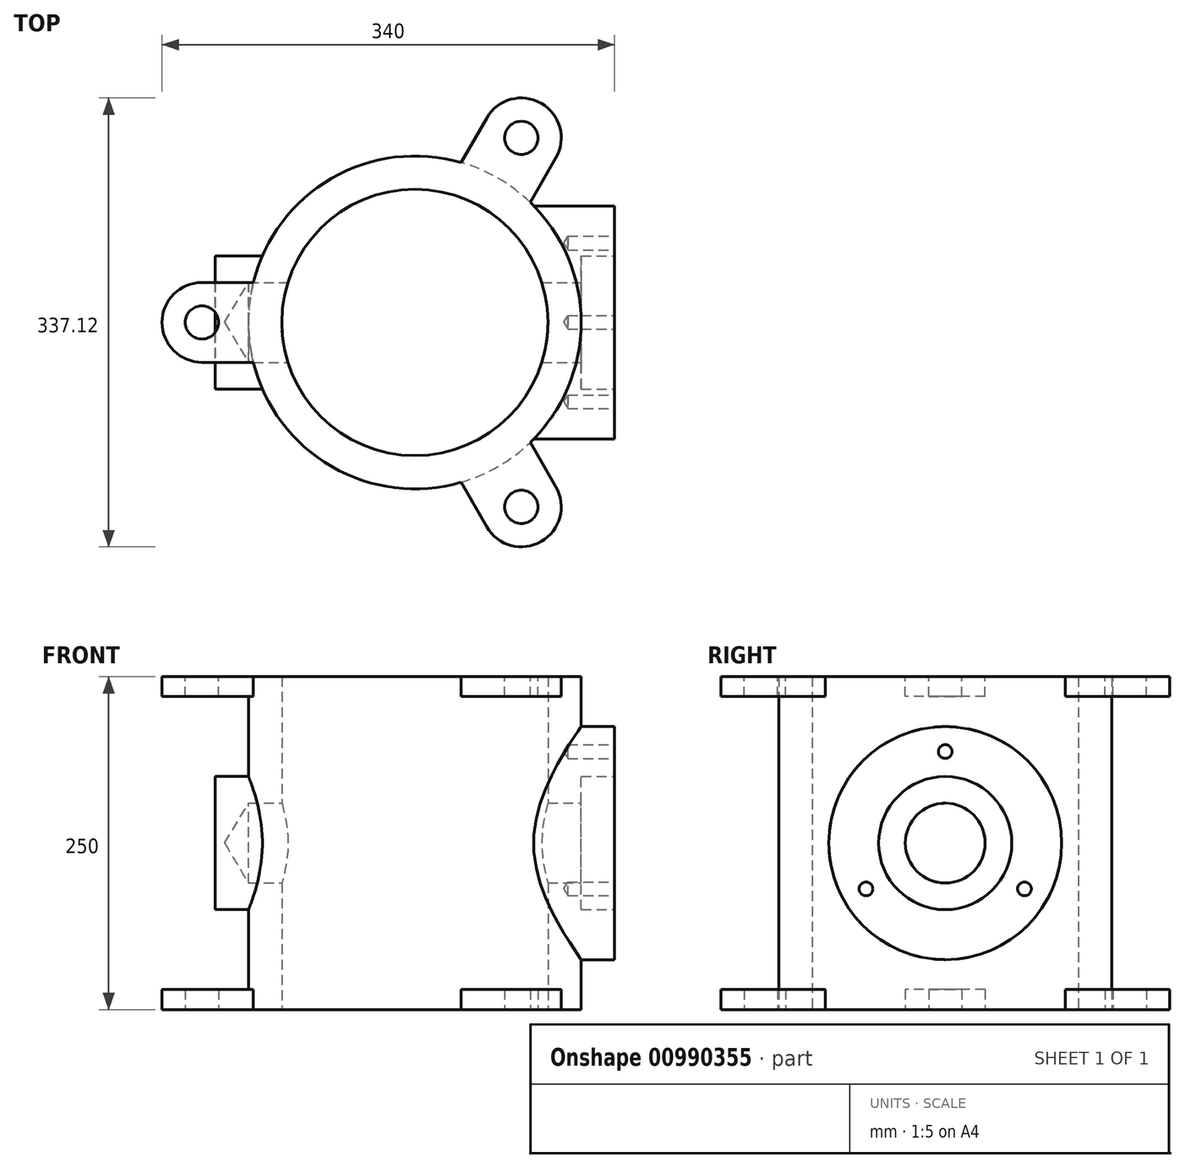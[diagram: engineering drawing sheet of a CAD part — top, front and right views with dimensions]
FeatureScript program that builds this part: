
annotation { "Feature Type Name" : "Feature", "Feature Type Description" : "" }
export const myFeature = defineFeature(function(context is Context, id is Id, definition is map)
    precondition{}
    {
        {
            var Q0;
            Q0=qCreatedBy(makeId("Top.planeOp"),FACE);
            cPlane(context, id + "F0", {"entities" : qUnion([Q0]), "cplaneType" : CPlaneType.OFFSET, "offset" : 125 * mm, "width" : 150 * mm, "height" : 150 * mm});
        }
        {
            var Q0;
            Q0=qCreatedBy(id+"F0.planeOp",FACE);
            var sketch = newSketch(context, id + "F1", { "sketchPlane" : qUnion([Q0])});
            skCircle(sketch, "E0", {"center": v(0, 0) * mm, "radius": 100 * mm});
            skCircle(sketch, "E1", {"center": v(0, 0) * mm, "radius": 125 * mm});
            skCircle(sketch, "E2", {"center": v(0, 0) * mm, "radius": 160 * mm, "construction": true});
            skLineSegment(sketch, "E3", {"start": v(0, 0) * mm, "end": v(-160, 0) * mm, "construction": true});
            skCircle(sketch, "E4", {"center": v(-160, 0) * mm, "radius": 12.5 * mm});
            skArc(sketch, "E5", {"start": v(-160, -30) * mm, "mid": v(-190, 0) * mm, "end": v(-160, 30) * mm});
            skLineSegment(sketch, "E6", {"start": v(-160, 0) * mm, "end": v(-160, 30) * mm, "construction": true});
            skLineSegment(sketch, "E7", {"start": v(-160, 30) * mm, "end": v(-95.4, 30) * mm});
            skLineSegment(sketch, "E8.MirrorCS", {"start": v(-160, -30) * mm, "end": v(-95.4, -30) * mm});
            skCircle(sketch, "E9.1.0", {"center": v(80, -138.56) * mm, "radius": 12.5 * mm});
            skLineSegment(sketch, "E9.1.1", {"start": v(105.98, -123.56) * mm, "end": v(73.68, -67.61) * mm});
            skArc(sketch, "E9.1.2", {"start": v(105.98, -123.56) * mm, "mid": v(95, -164.54) * mm, "end": v(54.02, -153.56) * mm});
            skLineSegment(sketch, "E9.1.3", {"start": v(54.02, -153.56) * mm, "end": v(21.72, -97.61) * mm});
            skCircle(sketch, "E9.2.0", {"center": v(80, 138.56) * mm, "radius": 12.5 * mm});
            skLineSegment(sketch, "E9.2.1", {"start": v(54.02, 153.56) * mm, "end": v(21.72, 97.61) * mm});
            skArc(sketch, "E9.2.2", {"start": v(54.02, 153.56) * mm, "mid": v(95, 164.54) * mm, "end": v(105.98, 123.56) * mm});
            skLineSegment(sketch, "E9.2.3", {"start": v(105.98, 123.56) * mm, "end": v(73.68, 67.61) * mm});
            skSolve(sketch);
        }
        {
            var Q0;
            Q0=qCreatedBy(makeId("Top.planeOp"),FACE);
            var sketch = newSketch(context, id + "F2", { "sketchPlane" : qUnion([Q0])});
            skCircle(sketch, "E10", {"center": v(0, 0) * mm, "radius": 100 * mm});
            skCircle(sketch, "E11", {"center": v(0, 0) * mm, "radius": 125 * mm});
            skSolve(sketch);
        }
        {
            var Q0;
            Q0=makeQuery(id+"F2.imprint","IMPRINT",FACE,{"disambiguationData":[TD([[makeQuery(id+"F2.imprint","IMPRINT",EDGE,{"derivedFrom":sQuery(id+"F2.wireOp",EDGE,"E10")}),-1.0]])]});
            extrude(context, id + "F3", {"entities" : qUnion([Q0]), "endBound" : BoundingType.SYMMETRIC, "depth" : 250 * mm, "offsetDistance" : 25 * mm});
        }
        {
            var Q0;
            Q0 = qSketchRegion(id + "F1", true);
            extrude(context, id + "F4", {"entities" : qUnion([Q0]), "operationType" : NewBodyOperationType.ADD, "oppositeDirection" : true, "depth" : 15 * mm, "offsetDistance" : 25 * mm});
        }
        {
            var Q0;
            Q0=makeQuery(id+"F3.opExtrude","SWEPT_BODY",BODY,{"disambiguationData":[OSD([sQuery(id+"F2.wireOp",EDGE,"E10"),sQuery(id+"F2.wireOp",EDGE,"E11")])]});
            var Q1;
            Q1=qCreatedBy(makeId("Top.planeOp"),FACE);
            mirror(context, id + "F5", {"operationType" : NewBodyOperationType.ADD, "entities" : qUnion([Q0]), "mirrorPlane" : qUnion([Q1])});
        }
        {
            var Q0;
            Q0=qCreatedBy(makeId("Right.planeOp"),FACE);
            cPlane(context, id + "F6", {"entities" : qUnion([Q0]), "cplaneType" : CPlaneType.OFFSET, "offset" : 150 * mm, "width" : 150 * mm, "height" : 150 * mm});
        }
        {
            var Q0;
            Q0=qCreatedBy(id+"F6.planeOp",FACE);
            var sketch = newSketch(context, id + "F7", { "sketchPlane" : qUnion([Q0])});
            skCircle(sketch, "E12", {"center": v(0, 0) * mm, "radius": 87.5 * mm});
            skCircle(sketch, "E13", {"center": v(0, 0) * mm, "radius": 68.75 * mm, "construction": true});
            skCircle(sketch, "E14", {"center": v(0, 0) * mm, "radius": 50 * mm});
            skCircle(sketch, "E15", {"center": v(0, 0) * mm, "radius": 30 * mm});
            skLineSegment(sketch, "E16", {"start": v(0, 0) * mm, "end": v(0, 68.75) * mm, "construction": true});
            skPoint(sketch, "E17", {"position": v(0, 68.75) * mm});
            skPoint(sketch, "E18.1.0", {"position": v(-59.54, -34.37) * mm});
            skPoint(sketch, "E18.2.0", {"position": v(59.54, -34.38) * mm});
            skSolve(sketch);
        }
        {
            var Q0;
            Q0=makeQuery(id+"F7.imprint","IMPRINT",FACE,{"disambiguationData":[TD([[makeQuery(id+"F7.imprint","IMPRINT",EDGE,{"derivedFrom":sQuery(id+"F7.wireOp",EDGE,"E14")}),1.0]])]});
            var Q1;
            Q1=makeQuery(id+"F7.imprint","IMPRINT",FACE,{"disambiguationData":[TD([[makeQuery(id+"F7.imprint","IMPRINT",EDGE,{"derivedFrom":sQuery(id+"F7.wireOp",EDGE,"E12")}),1.0]])]});
            extrude(context, id + "F8", {"entities" : qUnion([Q0, Q1]), "operationType" : NewBodyOperationType.ADD, "endBound" : BoundingType.UP_TO_NEXT, "oppositeDirection" : true, "depth" : 25 * mm, "offsetDistance" : 25 * mm});
        }
        {
            var Q0;
            Q0=makeQuery(id+"F7.imprint","IMPRINT",FACE,{"disambiguationData":[TD([[makeQuery(id+"F7.imprint","IMPRINT",EDGE,{"derivedFrom":sQuery(id+"F7.wireOp",EDGE,"E14")}),1.0]])]});
            extrude(context, id + "F9", {"entities" : qUnion([Q0]), "operationType" : NewBodyOperationType.REMOVE, "oppositeDirection" : true, "depth" : 25 * mm, "offsetDistance" : 25 * mm});
        }
        {
            var Q0;
            Q0=sQuery(id+"F7.wireOp",VERTEX,"E17");
            var Q1;
            Q1=sQuery(id+"F7.wireOp",VERTEX,"E18.2.0");
            var Q2;
            Q2=sQuery(id+"F7.wireOp",VERTEX,"E18.1.0");
            var Q3;
            Q3=makeQuery(id+"F3.opExtrude","SWEPT_BODY",BODY,{"disambiguationData":[OSD([sQuery(id+"F2.wireOp",EDGE,"E10"),sQuery(id+"F2.wireOp",EDGE,"E11")])]});
            hole(context, id + "F10", {"style" : HoleStyle.SIMPLE, "endStyle" : HoleEndStyle.BLIND, "holeDiameter" : 10.3 * mm, "majorDiameter" : 5 * mm, "holeDepth" : 35 * mm, "isTappedThrough" : true, "tappedDepth" : 12 * mm, "tapClearance" : 3, "locations" : qUnion([Q0, Q1, Q2]), "scope" : qUnion([Q3])});
        }
        {
            var Q0;
            Q0=qCreatedBy(makeId("Right.planeOp"),FACE);
            cPlane(context, id + "F11", {"entities" : qUnion([Q0]), "cplaneType" : CPlaneType.OFFSET, "offset" : 150 * mm, "oppositeDirection" : true, "width" : 150 * mm, "height" : 150 * mm});
        }
        {
            var Q0;
            Q0=qCreatedBy(id+"F11.planeOp",FACE);
            var sketch = newSketch(context, id + "F12", { "sketchPlane" : qUnion([Q0])});
            skCircle(sketch, "E19", {"center": v(0, 0) * mm, "radius": 50 * mm});
            skSolve(sketch);
        }
        {
            var Q0;
            Q0 = qSketchRegion(id + "F12", true);
            extrude(context, id + "F13", {"entities" : qUnion([Q0]), "operationType" : NewBodyOperationType.ADD, "endBound" : BoundingType.UP_TO_NEXT, "depth" : 25 * mm, "offsetDistance" : 25 * mm});
        }
        {
            var Q0;
            Q0=sQuery(id+"F7.wireOp",VERTEX,"E12.center");
            var Q1;
            Q1=makeQuery(id+"F3.opExtrude","SWEPT_BODY",BODY,{"disambiguationData":[OSD([sQuery(id+"F2.wireOp",EDGE,"E10"),sQuery(id+"F2.wireOp",EDGE,"E11")])]});
            hole(context, id + "F14", {"style" : HoleStyle.C_BORE, "endStyle" : HoleEndStyle.BLIND, "holeDiameter" : 60 * mm, "cBoreDiameter" : 60 * mm, "cBoreDepth" : 25 * mm, "majorDiameter" : 5 * mm, "holeDepth" : 250 * mm, "isTappedThrough" : true, "tappedDepth" : 12 * mm, "tapClearance" : 3, "locations" : qUnion([Q0]), "scope" : qUnion([Q1])});
        }
    });
